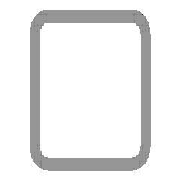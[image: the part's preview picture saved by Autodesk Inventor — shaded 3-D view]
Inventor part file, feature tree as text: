
AUTODESK INVENTOR PART (.ipt)
format: ipt  version: 2025.1 (Build 291241020, 241B)  size: 142,336 bytes
history: native  units: mm (DEFAULTED — no unit token found)
features: other x4, sketch x1, plane x1
ambient origin geometry x8: Origin, YZ Plane, XZ Plane, XY Plane, X Axis, Y Axis, Z Axis, Center Point
bodies: Solid1 (feature_tree), Body (feature_tree)
feature tree (6):
  parser-record x1  (decoder bookkeeping rows leaked as tree rows — omitted from the tree; the rows remain in map.json)
  other  "Driven Length"
  other  "Start Plane"
  other  "End Plane"
  sketch  "Sketch3"  dims[d3=1150.0mm d4=0.0mm d7=4.0mm d9=40.0mm d11=40.0mm d12=2.0mm d13=50.0mm d14=1200.0mm d15=20.0mm d16=20.0mm d17=90.0deg d18=1150.0mm]
  plane  "Work Plane3"
